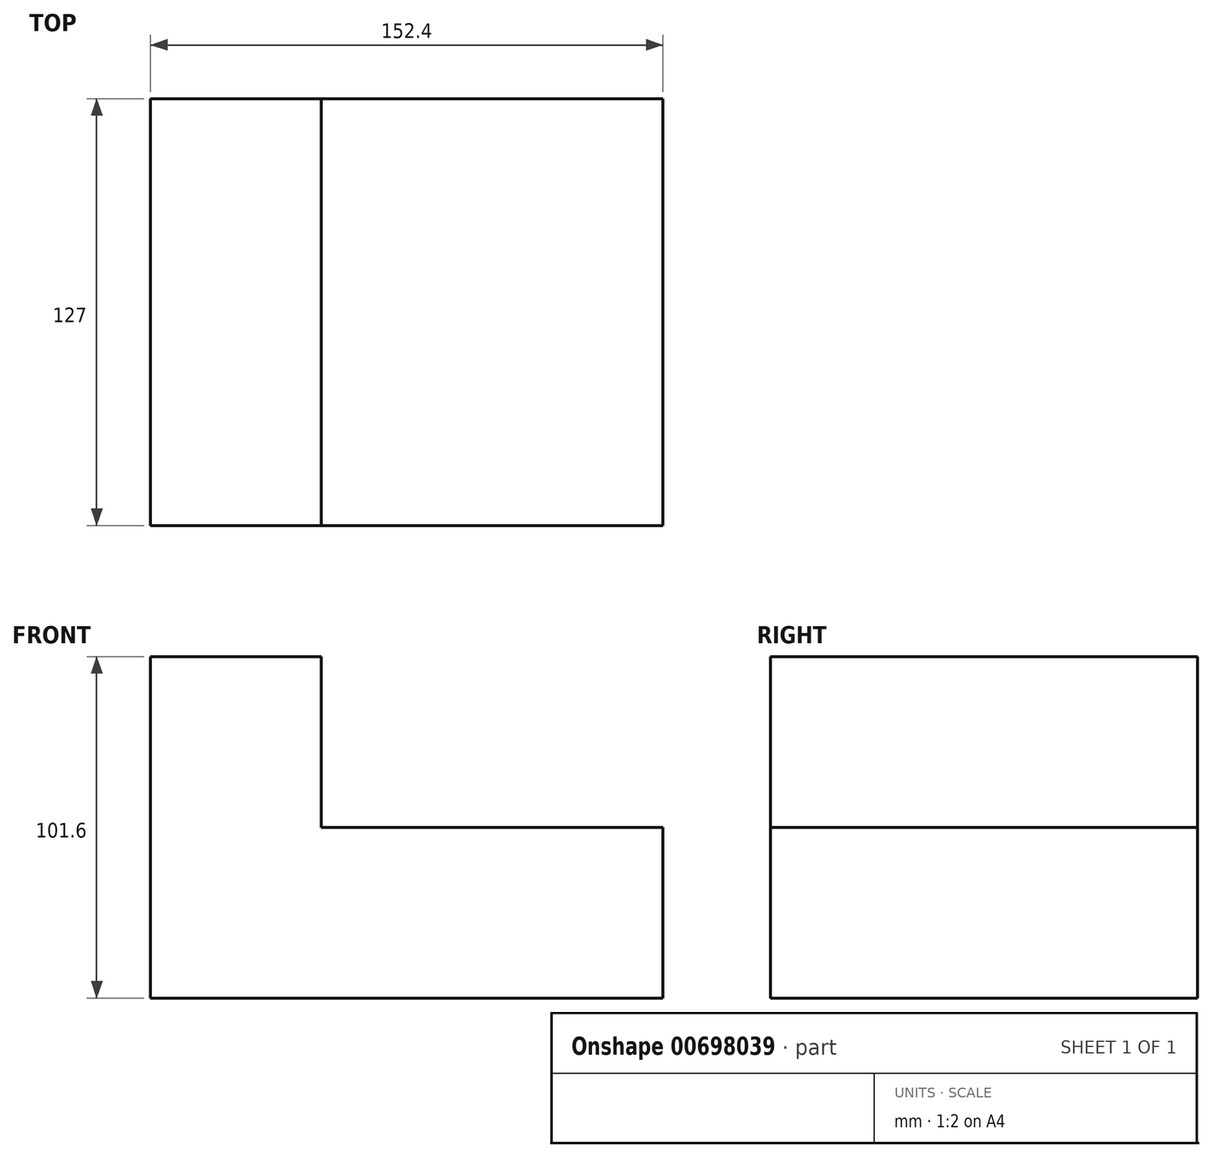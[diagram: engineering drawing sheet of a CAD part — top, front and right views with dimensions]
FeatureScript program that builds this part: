
annotation { "Feature Type Name" : "Feature", "Feature Type Description" : "" }
export const myFeature = defineFeature(function(context is Context, id is Id, definition is map)
    precondition{}
    {
        {
            var Q0;
            Q0=qCreatedBy(makeId("Front.planeOp"),FACE);
            var sketch = newSketch(context, id + "F0", { "sketchPlane" : qUnion([Q0])});
            skLineSegment(sketch, "E0", {"start": v(-135.64, -68.48) * mm, "end": v(16.76, -68.48) * mm});
            skLineSegment(sketch, "E1", {"start": v(16.76, -68.48) * mm, "end": v(16.76, -17.68) * mm});
            skLineSegment(sketch, "E2", {"start": v(16.76, -17.68) * mm, "end": v(-84.84, -17.68) * mm});
            skLineSegment(sketch, "E3", {"start": v(-84.84, -17.68) * mm, "end": v(-84.84, 33.12) * mm});
            skLineSegment(sketch, "E4", {"start": v(-84.84, 33.12) * mm, "end": v(-135.64, 33.12) * mm});
            skLineSegment(sketch, "E5", {"start": v(-135.64, 33.12) * mm, "end": v(-135.64, -68.48) * mm});
            skSolve(sketch);
        }
        {
            var Q0;
            Q0=makeQuery(id+"F0.imprint","IMPRINT",FACE,{"disambiguationData":[TD([[makeQuery(id+"F0.imprint","IMPRINT",EDGE,{"derivedFrom":sQuery(id+"F0.wireOp",EDGE,"E0")}),1.0]])]});
            extrude(context, id + "F1", {"entities" : qUnion([Q0]), "depth" : 127 * mm, "offsetDistance" : 25.4 * mm});
        }
    });
